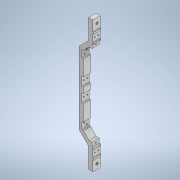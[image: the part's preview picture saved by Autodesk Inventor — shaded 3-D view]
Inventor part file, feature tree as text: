
AUTODESK INVENTOR PART (.ipt)
format: ipt  version: 2020 (Build 240168000, 168)  size: 435,712 bytes
history: native  units: mm
features: sketch x5, hole x5, projected_geometry x4, other x3, extrude x1
ambient origin geometry x8: Origin, YZ Plane, XZ Plane, XY Plane, X Axis, Y Axis, Z Axis, Center Point
bodies: Body1 (feature_tree)
feature tree (18):
  other  "솔리드1"
  other  "작업 평면1"
  extrude  "arch1"  Depth=20.0mm TaperAngle=0.0deg
  sketch  "스케치23"
  hole  "구멍11"  [1 undecoded]
  other  "작업 평면5"
  hole  "구멍12"  [1 undecoded]
  hole  "구멍14"  [1 undecoded]
  hole  "구멍16"  [1 undecoded]
  hole  "구멍18"  [1 undecoded]
  sketch  "스케치24"
  projected_geometry  "투영된 루프30"
  sketch  "스케치27"
  sketch  "스케치29"
  projected_geometry  "투영된 루프34"
  sketch  "스케치31"
  projected_geometry  "투영된 루프37"
  projected_geometry  "투영된 루프38"
note: 5 required parameter values undecoded (feature->parameter linkage not recoverable at this tier; creation-order binding heuristic only, values carry confidence <= 0.55)
